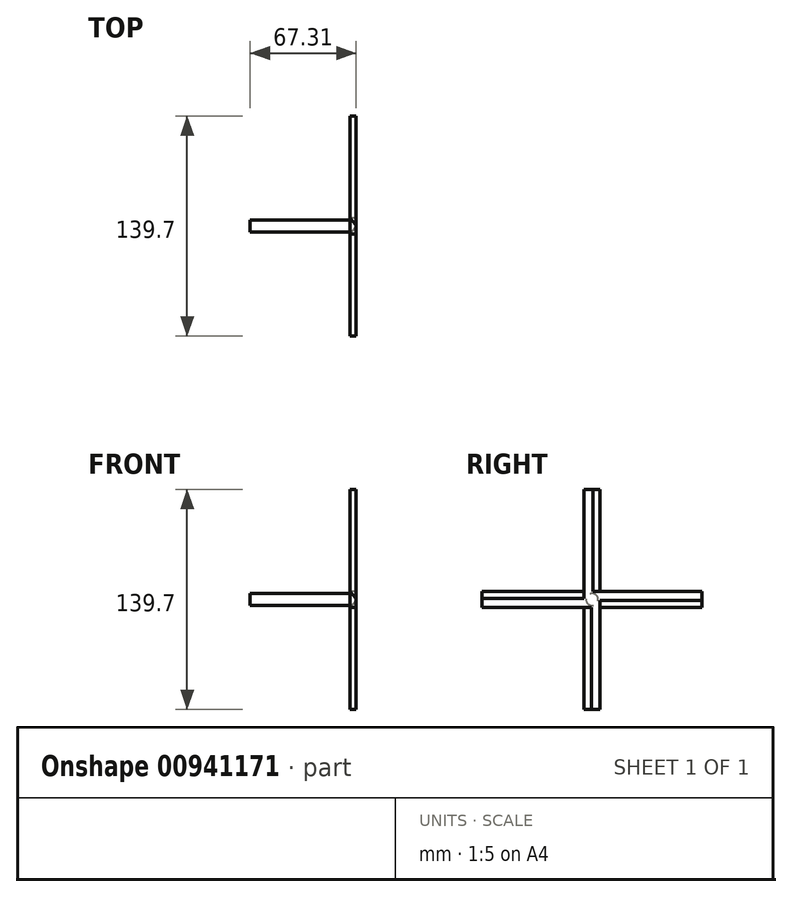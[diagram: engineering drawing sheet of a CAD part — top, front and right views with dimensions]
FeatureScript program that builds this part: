
annotation { "Feature Type Name" : "Feature", "Feature Type Description" : "" }
export const myFeature = defineFeature(function(context is Context, id is Id, definition is map)
    precondition{}
    {
        {
            var Q0;
            Q0=qCreatedBy(makeId("Right.planeOp"),FACE);
            var sketch = newSketch(context, id + "F0", { "sketchPlane" : qUnion([Q0])});
            skCircle(sketch, "E0", {"center": v(0, 0) * mm, "radius": 3.81 * mm});
            skSolve(sketch);
        }
        {
            var Q0;
            Q0 = qSketchRegion(id + "F0", true);
            extrude(context, id + "F1", {"entities" : qUnion([Q0]), "depth" : 12.7 * mm, "offsetDistance" : 25.4 * mm, "hasSecondDirection" : true, "secondDirectionOppositeDirection" : true, "secondDirectionDepth" : 50.8 * mm});
        }
        {
            var Q0;
            Q0=makeQuery(id+"F1.opExtrude","CAP_FACE",FACE,{"disambiguationData":[OSD([sQuery(id+"F0.wireOp",EDGE,"E0")])],"isStart":false});
            var sketch = newSketch(context, id + "F2", { "sketchPlane" : qUnion([Q0])});
            skLineSegment(sketch, "E1.bottom", {"start": v(69.85, 5.08) * mm, "end": v(-69.85, 5.08) * mm});
            skLineSegment(sketch, "E1.top", {"start": v(69.85, -5.08) * mm, "end": v(-69.85, -5.08) * mm});
            skLineSegment(sketch, "E1.left", {"start": v(69.85, 5.08) * mm, "end": v(69.85, -5.08) * mm});
            skLineSegment(sketch, "E1.right", {"start": v(-69.85, 5.08) * mm, "end": v(-69.85, -5.08) * mm});
            skPoint(sketch, "E1.middle", {"position": v(0, 0) * mm});
            skLineSegment(sketch, "E2.bottom", {"start": v(5.08, 69.85) * mm, "end": v(-5.08, 69.85) * mm});
            skLineSegment(sketch, "E2.top", {"start": v(5.08, -69.85) * mm, "end": v(-5.08, -69.85) * mm});
            skLineSegment(sketch, "E2.left", {"start": v(5.08, 69.85) * mm, "end": v(5.08, -69.85) * mm});
            skLineSegment(sketch, "E2.right", {"start": v(-5.08, 69.85) * mm, "end": v(-5.08, -69.85) * mm});
            skSolve(sketch);
        }
        {
            var Q0;
            Q0 = qSketchRegion(id + "F2", true);
            extrude(context, id + "F3", {"entities" : qUnion([Q0]), "operationType" : NewBodyOperationType.ADD, "depth" : 3.8 * mm, "offsetDistance" : 25.4 * mm});
        }
        {
            var Q0;
            {var subQ0=sQuery(id+"F2.wireOp",EDGE,"E2.left");Q0=makeQuery(id+"F3.opExtrude","CAP_EDGE",EDGE,{"disambiguationData":[OSD([subQ0]),TDD([makeQuery(id+"F2.imprint","IMPRINT",EDGE,{"disambiguationData":[TD([[makeQuery(id+"F2.imprint","INTERSECT",VERTEX,{"derivedFrom":[sQuery(id+"F2.wireOp",EDGE,"E2.bottom"),subQ0]}),-1.0]])],"derivedFrom":subQ0})])],"isStart":false});}
            var Q1;
            {var subQ0=sQuery(id+"F2.wireOp",EDGE,"E1.top");Q1=makeQuery(id+"F3.opExtrude","CAP_EDGE",EDGE,{"disambiguationData":[OSD([subQ0]),TDD([makeQuery(id+"F2.imprint","IMPRINT",EDGE,{"disambiguationData":[TD([[makeQuery(id+"F2.imprint","INTERSECT",VERTEX,{"derivedFrom":[subQ0,sQuery(id+"F2.wireOp",EDGE,"E1.left")]}),-1.0]])],"derivedFrom":subQ0})])],"isStart":false});}
            var Q2;
            {var subQ0=sQuery(id+"F2.wireOp",EDGE,"E2.right");Q2=makeQuery(id+"F3.opExtrude","CAP_EDGE",EDGE,{"disambiguationData":[OSD([subQ0]),TDD([makeQuery(id+"F2.imprint","IMPRINT",EDGE,{"disambiguationData":[TD([[makeQuery(id+"F2.imprint","INTERSECT",VERTEX,{"derivedFrom":[sQuery(id+"F2.wireOp",EDGE,"E2.top"),subQ0]}),1.0]])],"derivedFrom":subQ0})])],"isStart":false});}
            var Q3;
            {var subQ0=sQuery(id+"F2.wireOp",EDGE,"E1.bottom");Q3=makeQuery(id+"F3.opExtrude","CAP_EDGE",EDGE,{"disambiguationData":[OSD([subQ0]),TDD([makeQuery(id+"F2.imprint","IMPRINT",EDGE,{"disambiguationData":[TD([[makeQuery(id+"F2.imprint","INTERSECT",VERTEX,{"derivedFrom":[subQ0,sQuery(id+"F2.wireOp",EDGE,"E1.right")]}),1.0]])],"derivedFrom":subQ0})])],"isStart":false});}
            chamfer(context, id + "F4", {"entities" : qUnion([Q0, Q1, Q2, Q3]), "chamferType" : ChamferType.OFFSET_ANGLE, "width" : 3.8 * mm, "oppositeDirection" : false, "angle" : 50 * degree, "tangentPropagation" : true});
        }
    });
